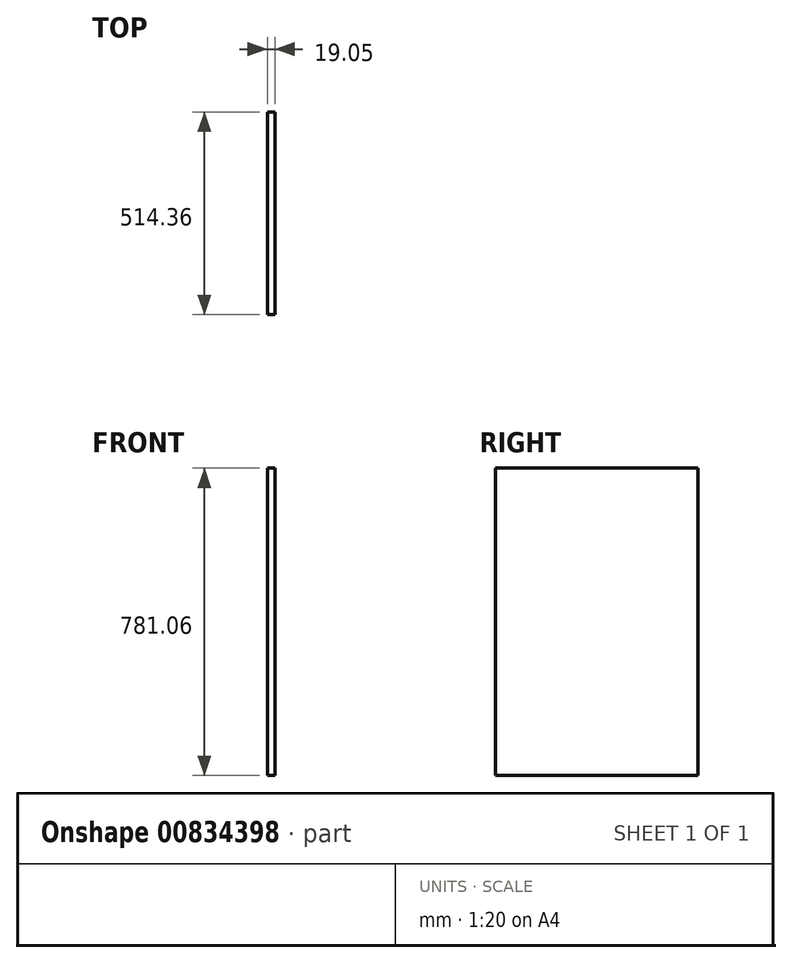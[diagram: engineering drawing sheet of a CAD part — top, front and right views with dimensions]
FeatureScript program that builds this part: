
annotation { "Feature Type Name" : "Feature", "Feature Type Description" : "" }
export const myFeature = defineFeature(function(context is Context, id is Id, definition is map)
    precondition{}
    {
        {
            var Q0;
            Q0=qCreatedBy(makeId("Right.planeOp"),FACE);
            var sketch = newSketch(context, id + "F0", { "sketchPlane" : qUnion([Q0])});
            skLineSegment(sketch, "E0.bottom", {"start": v(257.18, -390.53) * mm, "end": v(-257.17, -390.53) * mm});
            skLineSegment(sketch, "E0.top", {"start": v(257.18, 390.53) * mm, "end": v(-257.18, 390.53) * mm});
            skLineSegment(sketch, "E0.left", {"start": v(257.18, -390.53) * mm, "end": v(257.18, 390.53) * mm});
            skLineSegment(sketch, "E0.right", {"start": v(-257.18, -390.53) * mm, "end": v(-257.18, 390.53) * mm});
            skSolve(sketch);
        }
        {
            var Q0;
            Q0=makeQuery(id+"F0.imprint","IMPRINT",FACE,{"disambiguationData":[TD([[makeQuery(id+"F0.imprint","IMPRINT",EDGE,{"derivedFrom":sQuery(id+"F0.wireOp",EDGE,"E0.bottom")}),-1.0]])]});
            extrude(context, id + "F1", {"entities" : qUnion([Q0]), "oppositeDirection" : true, "depth" : 19.05 * mm, "offsetDistance" : 25.4 * mm});
        }
    });
